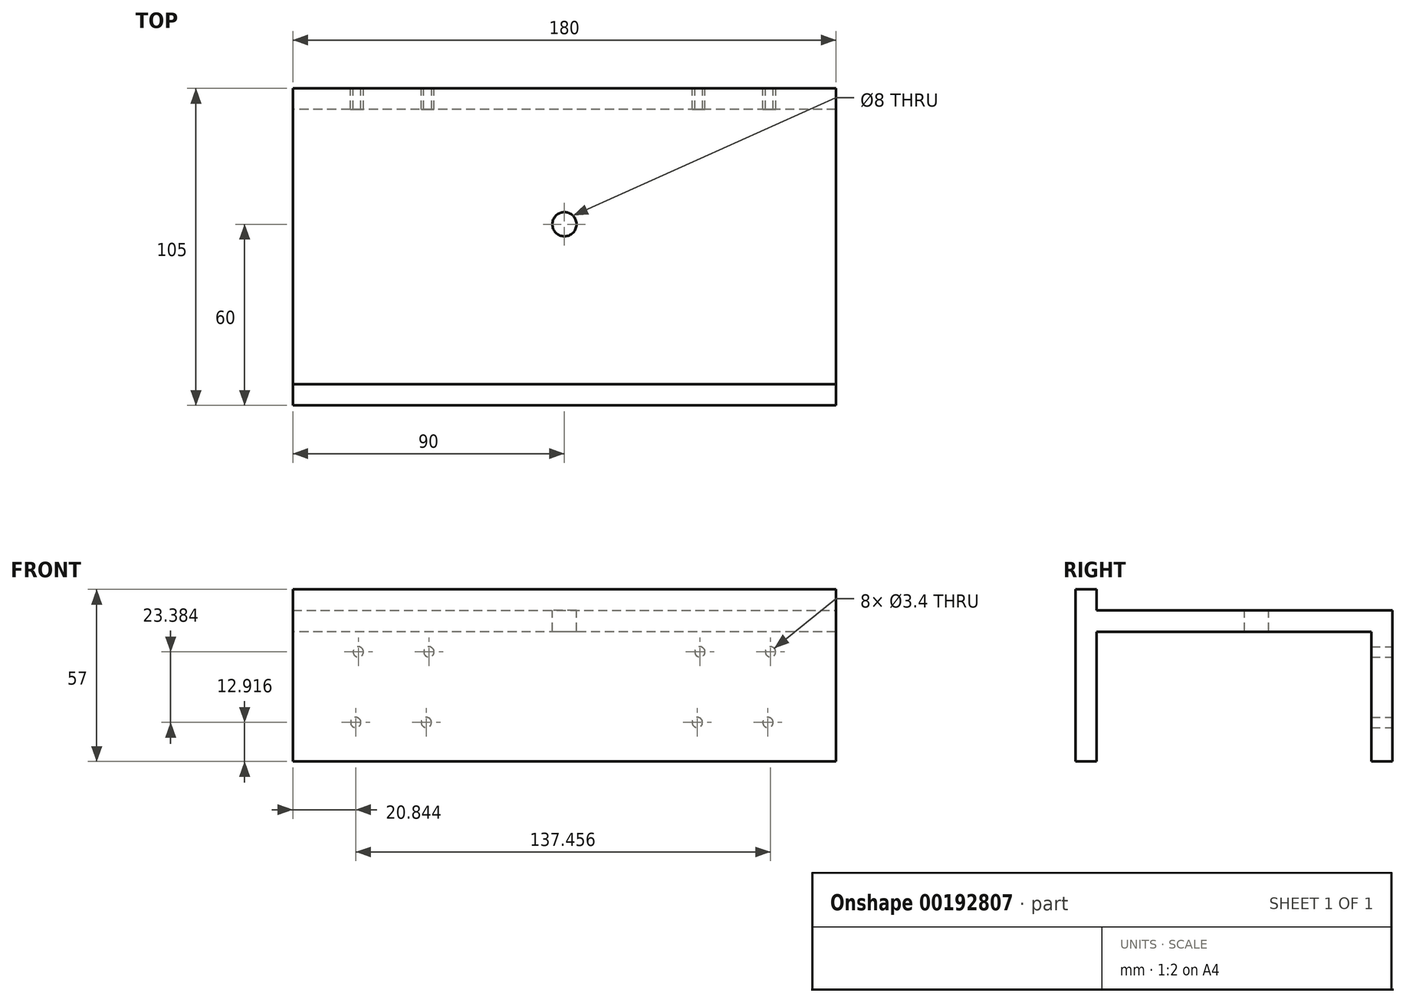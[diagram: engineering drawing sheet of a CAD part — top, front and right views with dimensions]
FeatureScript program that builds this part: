
annotation { "Feature Type Name" : "Feature", "Feature Type Description" : "" }
export const myFeature = defineFeature(function(context is Context, id is Id, definition is map)
    precondition{}
    {
        {
            var Q0;
            Q0=qCreatedBy(makeId("Top.planeOp"),FACE);
            var sketch = newSketch(context, id + "F0", { "sketchPlane" : qUnion([Q0])});
            skLineSegment(sketch, "E0.bottom", {"start": v(90, 52.5) * mm, "end": v(-90, 52.5) * mm});
            skLineSegment(sketch, "E0.top", {"start": v(90, -52.5) * mm, "end": v(-90, -52.5) * mm});
            skLineSegment(sketch, "E0.left", {"start": v(90, 52.5) * mm, "end": v(90, -52.5) * mm});
            skLineSegment(sketch, "E0.right", {"start": v(-90, 52.5) * mm, "end": v(-90, -52.5) * mm});
            skPoint(sketch, "E0.middle", {"position": v(0, 0) * mm});
            skSolve(sketch);
        }
        {
            var Q0;
            Q0 = qSketchRegion(id + "F0", true);
            extrude(context, id + "F1", {"entities" : qUnion([Q0]), "depth" : 50 * mm});
        }
        {
            var Q0;
            Q0=makeQuery(id+"F0.imprint","IMPRINT",FACE,{"disambiguationData":[TD([[makeQuery(id+"F0.imprint","IMPRINT",EDGE,{"derivedFrom":sQuery(id+"F0.wireOp",EDGE,"E0.bottom")}),1.0]])]});
            var sketch = newSketch(context, id + "F2", { "sketchPlane" : qUnion([Q0])});
            skLineSegment(sketch, "E1.bottom", {"start": v(90, -45.5) * mm, "end": v(-90, -45.5) * mm});
            skLineSegment(sketch, "E1.top", {"start": v(90, 45.5) * mm, "end": v(-90, 45.5) * mm});
            skLineSegment(sketch, "E1.left", {"start": v(90, -45.5) * mm, "end": v(90, 45.5) * mm});
            skLineSegment(sketch, "E1.right", {"start": v(-90, -45.5) * mm, "end": v(-90, 45.5) * mm});
            skPoint(sketch, "E1.middle", {"position": v(0, 0) * mm});
            skSolve(sketch);
        }
        {
            var Q0;
            Q0 = qSketchRegion(id + "F2", true);
            extrude(context, id + "F3", {"entities" : qUnion([Q0]), "operationType" : NewBodyOperationType.REMOVE, "oppositeDirection" : true, "depth" : 1 * mm, "hasSecondDirection" : true, "secondDirectionOppositeDirection" : false, "secondDirectionDepth" : 43 * mm});
        }
        {
            var Q0;
            Q0=makeQuery(id+"F1.opExtrude","CAP_FACE",FACE,{"disambiguationData":[OSD([sQuery(id+"F0.wireOp",EDGE,"E0.bottom"),sQuery(id+"F0.wireOp",EDGE,"E0.top"),sQuery(id+"F0.wireOp",EDGE,"E0.left"),sQuery(id+"F0.wireOp",EDGE,"E0.right")])],"isStart":false});
            var sketch = newSketch(context, id + "F4", { "sketchPlane" : qUnion([Q0])});
            skCircle(sketch, "E2", {"center": v(0, 7.5) * mm, "radius": 4 * mm});
            skSolve(sketch);
        }
        {
            var Q0;
            Q0 = qSketchRegion(id + "F4", true);
            extrude(context, id + "F5", {"entities" : qUnion([Q0]), "operationType" : NewBodyOperationType.REMOVE, "endBound" : BoundingType.THROUGH_ALL, "oppositeDirection" : true, "depth" : 25 * mm});
        }
        {
            var Q0;
            Q0=makeQuery(id+"F1.opExtrude","CAP_FACE",FACE,{"disambiguationData":[OSD([sQuery(id+"F0.wireOp",EDGE,"E0.bottom"),sQuery(id+"F0.wireOp",EDGE,"E0.top"),sQuery(id+"F0.wireOp",EDGE,"E0.left"),sQuery(id+"F0.wireOp",EDGE,"E0.right")])],"isStart":false});
            var sketch = newSketch(context, id + "F6", { "sketchPlane" : qUnion([Q0])});
            skLineSegment(sketch, "E3.bottom", {"start": v(-90, -52.5) * mm, "end": v(90, -52.5) * mm});
            skLineSegment(sketch, "E3.top", {"start": v(-90, -45.5) * mm, "end": v(90, -45.5) * mm});
            skLineSegment(sketch, "E3.left", {"start": v(-90, -52.5) * mm, "end": v(-90, -45.5) * mm});
            skLineSegment(sketch, "E3.right", {"start": v(90, -52.5) * mm, "end": v(90, -45.5) * mm});
            skSolve(sketch);
        }
        {
            var Q0;
            Q0 = qSketchRegion(id + "F6", true);
            extrude(context, id + "F7", {"entities" : qUnion([Q0]), "operationType" : NewBodyOperationType.ADD, "depth" : 7 * mm});
        }
        {
            var Q0;
            Q0=makeQuery(id+"F1.opExtrude","SWEPT_FACE",FACE,{"disambiguationData":[OSD([sQuery(id+"F0.wireOp",EDGE,"E0.bottom")])]});
            var sketch = newSketch(context, id + "F8", { "sketchPlane" : qUnion([Q0])});
            skCircle(sketch, "E4", {"center": v(-68.3, 36.3) * mm, "radius": 1.7 * mm});
            skCircle(sketch, "E5", {"center": v(-67.44, 12.92) * mm, "radius": 1.7 * mm});
            skCircle(sketch, "E6", {"center": v(-44.9, 36.3) * mm, "radius": 1.7 * mm});
            skCircle(sketch, "E7", {"center": v(-44.04, 12.92) * mm, "radius": 1.7 * mm});
            skCircle(sketch, "E8", {"center": v(44.9, 36.3) * mm, "radius": 1.7 * mm});
            skCircle(sketch, "E9", {"center": v(45.76, 12.92) * mm, "radius": 1.7 * mm});
            skCircle(sketch, "E10", {"center": v(68.3, 36.3) * mm, "radius": 1.7 * mm});
            skCircle(sketch, "E11", {"center": v(69.16, 12.92) * mm, "radius": 1.7 * mm});
            skSolve(sketch);
        }
        {
            var Q0;
            Q0 = qSketchRegion(id + "F8", true);
            var Q1;
            Q1=makeQuery(id+"F3.boolean.opBoolean","COPY",FACE,{"derivedFrom":makeQuery(id+"F3.opExtrude","SWEPT_FACE",FACE,{"disambiguationData":[OSD([sQuery(id+"F2.wireOp",EDGE,"E1.top")])]})});
            extrude(context, id + "F9", {"entities" : qUnion([Q0]), "operationType" : NewBodyOperationType.REMOVE, "endBound" : BoundingType.UP_TO_SURFACE, "oppositeDirection" : true, "endBoundEntityFace" : qUnion([Q1]), "depth" : 25 * mm});
        }
    });
